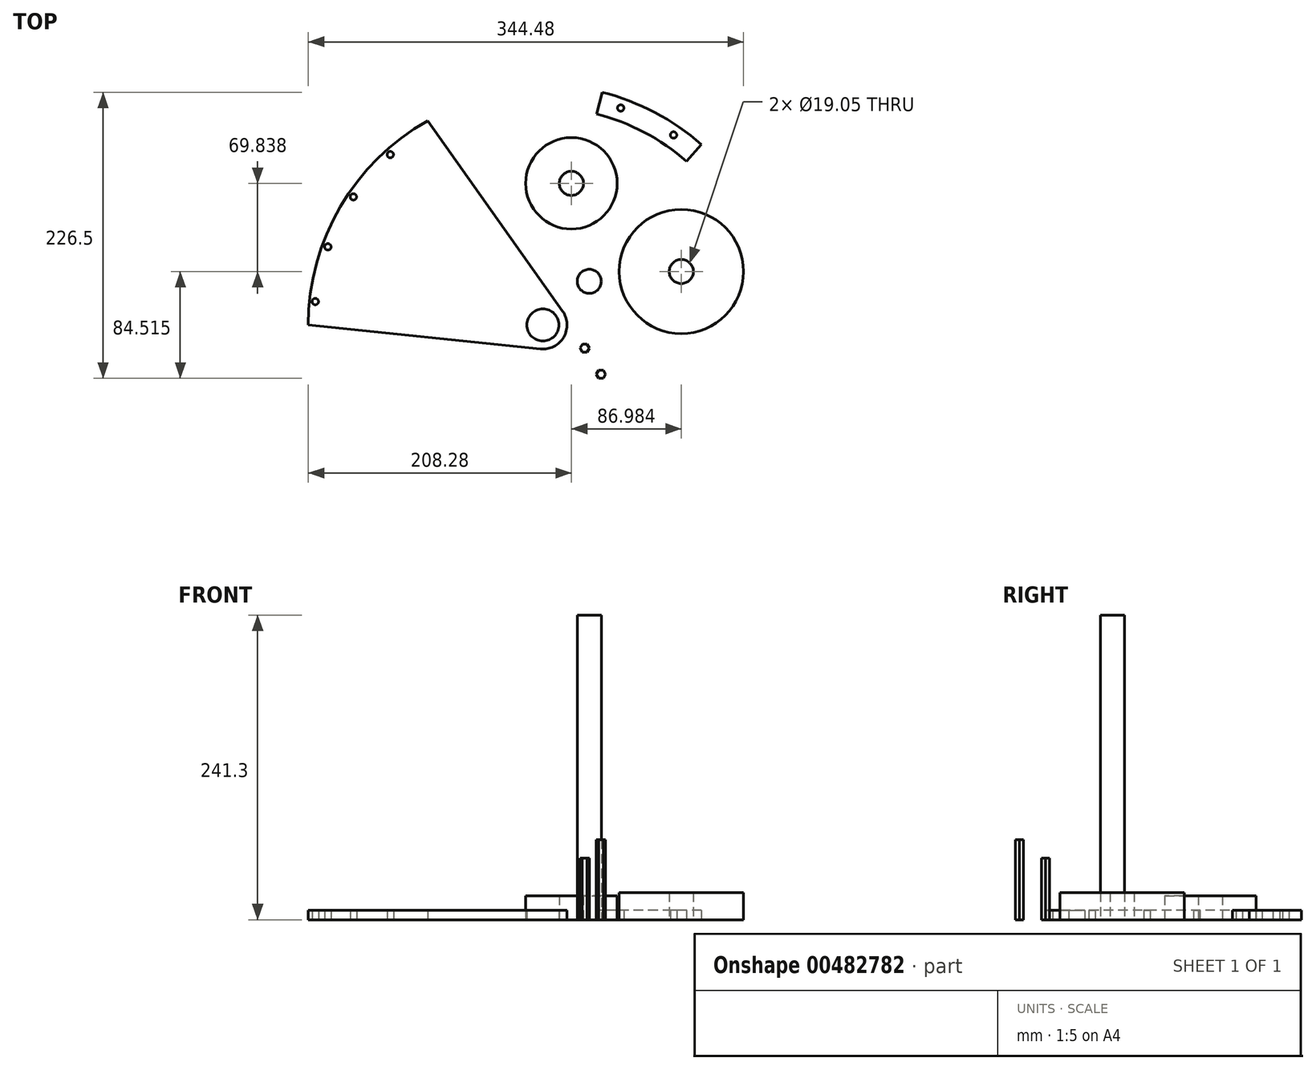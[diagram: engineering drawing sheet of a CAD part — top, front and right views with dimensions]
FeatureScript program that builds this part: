
annotation { "Feature Type Name" : "Feature", "Feature Type Description" : "" }
export const myFeature = defineFeature(function(context is Context, id is Id, definition is map)
    precondition{}
    {
        {
            var Q0;
            Q0=qCreatedBy(makeId("Top.planeOp"),FACE);
            var sketch = newSketch(context, id + "F0", { "sketchPlane" : qUnion([Q0])});
            skCircle(sketch, "E0", {"center": v(0, 0) * mm, "radius": 12.7 * mm});
            skCircle(sketch, "E1", {"center": v(0, 0) * mm, "radius": 9.53 * mm});
            skArc(sketch, "E2", {"start": v(-1.95, -18.95) * mm, "mid": v(16.45, -9.6) * mm, "end": v(15.54, 11.01) * mm});
            skArc(sketch, "E3", {"start": v(-91.27, 161.76) * mm, "mid": v(-160.4, 93.66) * mm, "end": v(-185.74, 0) * mm});
            skLineSegment(sketch, "E4", {"start": v(-91.27, 161.76) * mm, "end": v(15.54, 11.01) * mm});
            skLineSegment(sketch, "E5", {"start": v(-185.74, 0) * mm, "end": v(-1.95, -18.95) * mm});
            skCircle(sketch, "E6", {"center": v(-180.19, 18.55) * mm, "radius": 2.54 * mm});
            skCircle(sketch, "E7", {"center": v(-170.24, 61.88) * mm, "radius": 2.54 * mm});
            skCircle(sketch, "E8", {"center": v(-150.05, 101.47) * mm, "radius": 2.54 * mm});
            skLineSegment(sketch, "E9", {"start": v(-150.05, 101.47) * mm, "end": v(-148.38, 103.39) * mm});
            skCircle(sketch, "E10", {"center": v(-120.82, 134.96) * mm, "radius": 2.54 * mm});
            skSolve(sketch);
        }
        {
            var Q0;
            Q0=makeQuery(id+"F0.imprint","IMPRINT",FACE,{"disambiguationData":[TD([[makeQuery(id+"F0.imprint","IMPRINT",EDGE,{"derivedFrom":sQuery(id+"F0.wireOp",EDGE,"E0")}),-1.0]])]});
            extrude(context, id + "F1", {"entities" : qUnion([Q0]), "depth" : 7.62 * mm});
        }
        {
            var Q0;
            Q0=qCreatedBy(makeId("Top.planeOp"),FACE);
            var sketch = newSketch(context, id + "F2", { "sketchPlane" : qUnion([Q0])});
            skCircle(sketch, "E11", {"center": v(36.65, 34.57) * mm, "radius": 9.53 * mm});
            skSolve(sketch);
        }
        {
            var Q0;
            Q0=makeQuery(id+"F2.imprint","IMPRINT",FACE,{"disambiguationData":[TD([[makeQuery(id+"F2.imprint","IMPRINT",EDGE,{"derivedFrom":sQuery(id+"F2.wireOp",EDGE,"E11")}),1.0]])]});
            extrude(context, id + "F3", {"entities" : qUnion([Q0]), "depth" : 241.3 * mm});
        }
        {
            var Q0;
            Q0=qCreatedBy(makeId("Top.planeOp"),FACE);
            var sketch = newSketch(context, id + "F4", { "sketchPlane" : qUnion([Q0])});
            skCircle(sketch, "E12", {"center": v(109.52, 42.35) * mm, "radius": 49.21 * mm});
            skCircle(sketch, "E13", {"center": v(109.52, 42.35) * mm, "radius": 9.53 * mm});
            skSolve(sketch);
        }
        {
            var Q0;
            Q0=makeQuery(id+"F4.imprint","IMPRINT",FACE,{"disambiguationData":[TD([[makeQuery(id+"F4.imprint","IMPRINT",EDGE,{"derivedFrom":sQuery(id+"F4.wireOp",EDGE,"E12")}),1.0]])]});
            extrude(context, id + "F5", {"entities" : qUnion([Q0]), "depth" : 21.59 * mm});
        }
        {
            var Q0;
            Q0=qCreatedBy(makeId("Top.planeOp"),FACE);
            var sketch = newSketch(context, id + "F6", { "sketchPlane" : qUnion([Q0])});
            skCircle(sketch, "E14.cCircle", {"center": v(33.09, -18.28) * mm, "radius": 3.18 * mm, "construction": true});
            skLineSegment(sketch, "E14.0", {"start": v(35.03, -15.17) * mm, "end": v(36.75, -18.4) * mm});
            skLineSegment(sketch, "E14.1", {"start": v(36.75, -18.4) * mm, "end": v(34.8, -21.52) * mm});
            skLineSegment(sketch, "E14.2", {"start": v(34.8, -21.52) * mm, "end": v(31.15, -21.39) * mm});
            skLineSegment(sketch, "E14.3", {"start": v(31.15, -21.39) * mm, "end": v(29.42, -18.15) * mm});
            skLineSegment(sketch, "E14.4", {"start": v(29.42, -18.15) * mm, "end": v(31.36, -15.04) * mm});
            skLineSegment(sketch, "E14.5", {"start": v(31.36, -15.04) * mm, "end": v(35.03, -15.17) * mm});
            skPoint(sketch, "E14.0.midPoint", {"position": v(35.89, -16.79) * mm});
            skSolve(sketch);
        }
        {
            var Q0;
            Q0=makeQuery(id+"F6.imprint","IMPRINT",FACE,{"disambiguationData":[TD([[makeQuery(id+"F6.imprint","IMPRINT",EDGE,{"derivedFrom":sQuery(id+"F6.wireOp",EDGE,"E14.0")}),-1.0]])]});
            extrude(context, id + "F7", {"entities" : qUnion([Q0]), "depth" : 48.9 * mm});
        }
        {
            var Q0;
            Q0=qCreatedBy(makeId("Top.planeOp"),FACE);
            var sketch = newSketch(context, id + "F8", { "sketchPlane" : qUnion([Q0])});
            skArc(sketch, "E15", {"start": v(125.47, 142.92) * mm, "mid": v(88.6, 168.29) * mm, "end": v(46.8, 184.33) * mm});
            skArc(sketch, "E16", {"start": v(113.74, 129.56) * mm, "mid": v(80.31, 152.55) * mm, "end": v(42.43, 167.1) * mm});
            skLineSegment(sketch, "E17", {"start": v(46.8, 184.33) * mm, "end": v(42.43, 167.1) * mm});
            skLineSegment(sketch, "E18", {"start": v(125.47, 142.92) * mm, "end": v(113.74, 129.56) * mm});
            skCircle(sketch, "E19", {"center": v(103.4, 150.45) * mm, "radius": 2.54 * mm});
            skCircle(sketch, "E20", {"center": v(61.58, 171.86) * mm, "radius": 2.54 * mm});
            skSolve(sketch);
        }
        {
            var Q0;
            Q0 = qSketchRegion(id + "F8", true);
            var Q1;
            Q1=makeQuery(id+"F8.imprint","IMPRINT",FACE,{"disambiguationData":[TD([[makeQuery(id+"F8.imprint","IMPRINT",EDGE,{"derivedFrom":sQuery(id+"F8.wireOp",EDGE,"E15")}),1.0]])]});
            extrude(context, id + "F9", {"entities" : qUnion([Q0, Q1]), "depth" : 7.62 * mm});
        }
        {
            var Q0;
            Q0=qCreatedBy(makeId("Top.planeOp"),FACE);
            var sketch = newSketch(context, id + "F10", { "sketchPlane" : qUnion([Q0])});
            skCircle(sketch, "E21.cCircle", {"center": v(45.97, -38.96) * mm, "radius": 3.18 * mm, "construction": true});
            skLineSegment(sketch, "E21.0", {"start": v(47.85, -35.82) * mm, "end": v(49.64, -39.02) * mm});
            skLineSegment(sketch, "E21.1", {"start": v(49.64, -39.02) * mm, "end": v(47.75, -42.17) * mm});
            skLineSegment(sketch, "E21.2", {"start": v(47.75, -42.17) * mm, "end": v(44.09, -42.1) * mm});
            skLineSegment(sketch, "E21.3", {"start": v(44.09, -42.1) * mm, "end": v(42.3, -38.9) * mm});
            skLineSegment(sketch, "E21.4", {"start": v(42.3, -38.9) * mm, "end": v(44.19, -35.76) * mm});
            skLineSegment(sketch, "E21.5", {"start": v(44.19, -35.76) * mm, "end": v(47.85, -35.82) * mm});
            skPoint(sketch, "E21.0.midPoint", {"position": v(48.74, -37.42) * mm});
            skSolve(sketch);
        }
        {
            var Q0;
            Q0 = qSketchRegion(id + "F10", true);
            var Q1;
            Q1=makeQuery(id+"F10.imprint","IMPRINT",FACE,{"disambiguationData":[TD([[makeQuery(id+"F10.imprint","IMPRINT",EDGE,{"derivedFrom":sQuery(id+"F10.wireOp",EDGE,"E21.0")}),-1.0]])]});
            extrude(context, id + "F11", {"entities" : qUnion([Q0, Q1]), "depth" : 63.5 * mm});
        }
        {
            var Q0;
            Q0=qCreatedBy(makeId("Top.planeOp"),FACE);
            var sketch = newSketch(context, id + "F12", { "sketchPlane" : qUnion([Q0])});
            skCircle(sketch, "E22", {"center": v(22.54, 112.18) * mm, "radius": 36.2 * mm});
            skCircle(sketch, "E23", {"center": v(22.54, 112.18) * mm, "radius": 9.53 * mm});
            skSolve(sketch);
        }
        {
            var Q0;
            Q0=makeQuery(id+"F12.imprint","IMPRINT",FACE,{"disambiguationData":[TD([[makeQuery(id+"F12.imprint","IMPRINT",EDGE,{"derivedFrom":sQuery(id+"F12.wireOp",EDGE,"E22")}),1.0]])]});
            extrude(context, id + "F13", {"entities" : qUnion([Q0]), "depth" : 19.05 * mm});
        }
    });
